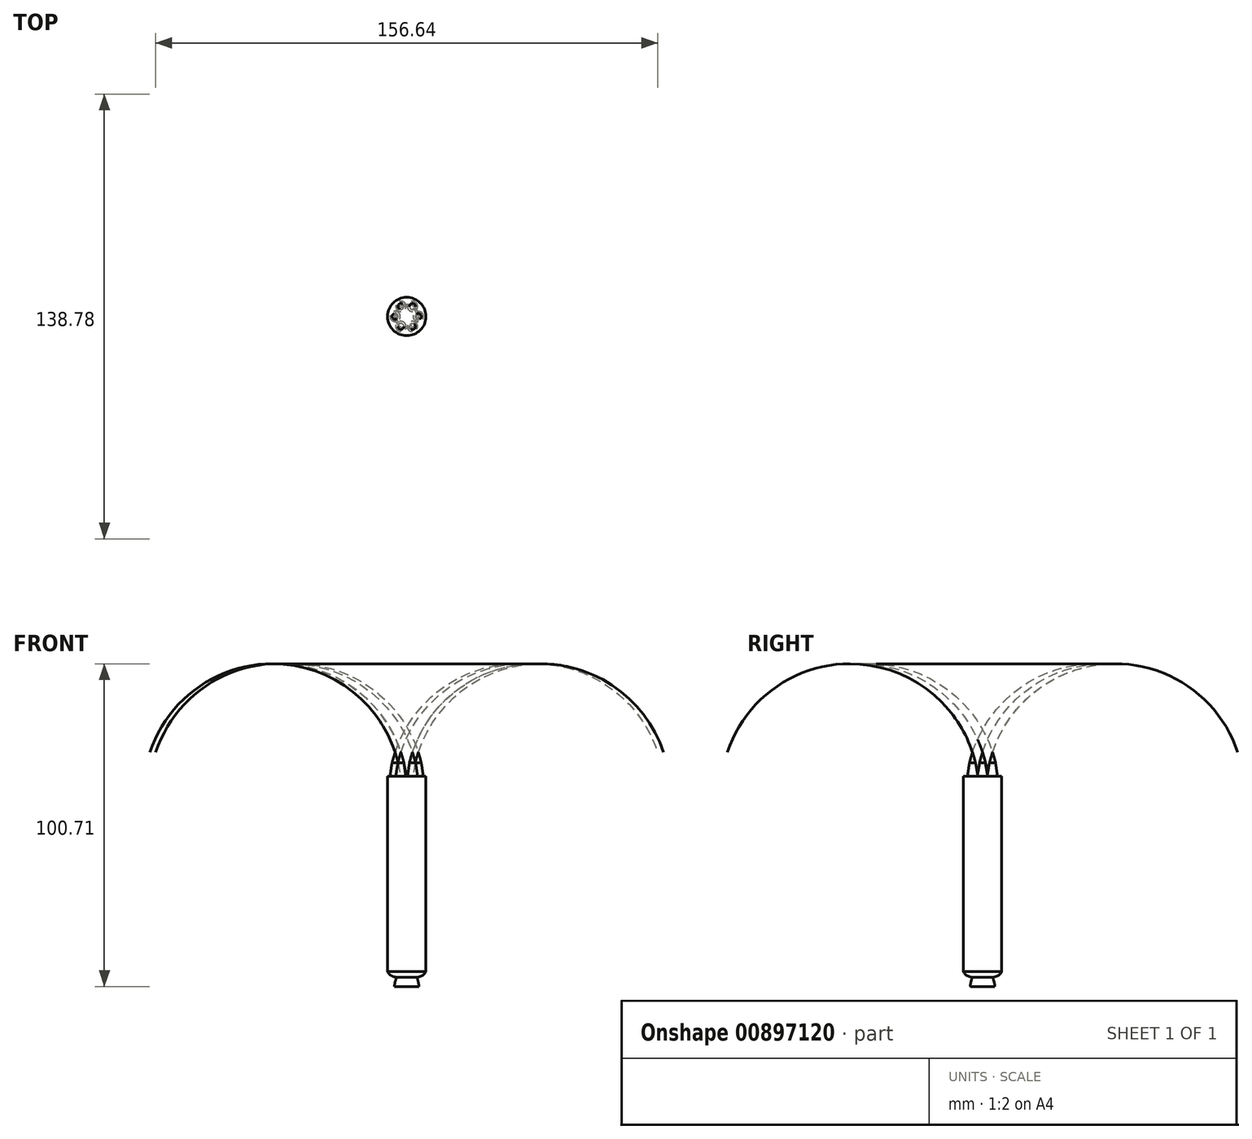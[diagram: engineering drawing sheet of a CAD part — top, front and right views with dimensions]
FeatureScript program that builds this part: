
annotation { "Feature Type Name" : "Feature", "Feature Type Description" : "" }
export const myFeature = defineFeature(function(context is Context, id is Id, definition is map)
    precondition{}
    {
        {
            var Q0;
            Q0=qCreatedBy(makeId("Front.planeOp"),FACE);
            var sketch = newSketch(context, id + "F0", { "sketchPlane" : qUnion([Q0])});
            skLineSegment(sketch, "E0", {"start": v(-6.84, -46.79) * mm, "end": v(-6.84, 46.23) * mm});
            skArc(sketch, "E1", {"start": v(-0.31, 41.1) * mm, "mid": v(-2.84, 44.6) * mm, "end": v(-6.84, 46.23) * mm});
            skFitSpline(sketch, "E2", {"points": [v(-0.84, -41.76) * mm, v(-3.65, -43.58) * mm], "startDerivative": vector(-1.75, -3.7) * mm, "endDerivative": vector(-3.13, -0.64) * mm});
            skFitSpline(sketch, "E3", {"points": [v(-3.65, -43.58) * mm, v(-3.08, -46.42) * mm], "startDerivative": vector(0.76, -2) * mm, "endDerivative": vector(-0.4, -1.8) * mm});
            skFitSpline(sketch, "E4", {"points": [v(-6.84, -46.79) * mm, v(-3.08, -46.42) * mm], "startDerivative": vector(2.11, -0.25) * mm, "endDerivative": vector(1.76, 0.6) * mm});
            skLineSegment(sketch, "E5", {"start": v(-0.81, 19.23) * mm, "end": v(-6.84, 19.23) * mm});
            skLineSegment(sketch, "E6", {"start": v(-6.84, -46.42) * mm, "end": v(-3.08, -46.42) * mm});
            skLineSegment(sketch, "E7", {"start": v(-0.84, -41.76) * mm, "end": v(-0.84, 19.23) * mm});
            skSolve(sketch);
        }
        {
            var Q0;
            Q0=makeQuery(id+"F0.imprint","IMPRINT",FACE,{"disambiguationData":[TD([[makeQuery(id+"F0.imprint","IMPRINT",EDGE,{"derivedFrom":sQuery(id+"F0.wireOp",EDGE,"3bf67111-f146-45a5-a568-fcc49153348b")}),-1.0]])]});
            var Q1;
            Q1=makeQuery(id+"F0.imprint","IMPRINT",FACE,{"disambiguationData":[TD([[makeQuery(id+"F0.imprint","IMPRINT",EDGE,{"derivedFrom":sQuery(id+"F0.wireOp",EDGE,"E2")}),-1.0]])]});
            var Q2;
            Q2=sQuery(id+"F0.wireOp",EDGE,"E0");
            revolve(context, id + "F1", {"surfaceOperationType" : NewSurfaceOperationType.NEW, "entities" : qUnion([Q0, Q1]), "axis" : qUnion([Q2]), "revolveType" : RevolveType.FULL});
        }
        {
            var Q0;
            Q0=makeQuery(id+"F1.opRevolve","SWEPT_FACE",FACE,{"disambiguationData":[OSD([sQuery(id+"F0.wireOp",EDGE,"E5")])]});
            var sketch = newSketch(context, id + "F2", { "sketchPlane" : qUnion([Q0])});
            skCircle(sketch, "E8", {"center": v(-6.84, 0.02) * mm, "radius": 6.5 * mm});
            skPoint(sketch, "E8.first.point", {"position": v(-13.33, -0.33) * mm});
            skPoint(sketch, "E8.second.point", {"position": v(-0.35, 0.35) * mm});
            skPoint(sketch, "E8.third.point", {"position": v(-0.56, -1.64) * mm});
            skCircle(sketch, "E9", {"center": v(-10.47, 0.02) * mm, "radius": 1.6 * mm});
            skCircle(sketch, "E10.1.0", {"center": v(-8.66, -3.12) * mm, "radius": 1.6 * mm});
            skCircle(sketch, "E10.2.0", {"center": v(-5.02, -3.12) * mm, "radius": 1.6 * mm});
            skCircle(sketch, "E10.3.0", {"center": v(-3.2, 0.02) * mm, "radius": 1.6 * mm});
            skCircle(sketch, "E10.4.0", {"center": v(-5.02, 3.17) * mm, "radius": 1.6 * mm});
            skCircle(sketch, "E10.5.0", {"center": v(-8.66, 3.17) * mm, "radius": 1.6 * mm});
            skPoint(sketch, "E11", {"position": v(-6.84, 0) * mm});
            skSolve(sketch);
        }
        {
            var Q0;
            Q0=sQuery(id+"F2.wireOp",EDGE,"E10.1.0");
            cPlane(context, id + "F3", {"entities" : qUnion([Q0]), "cplaneType" : CPlaneType.LINE_ANGLE, "offset" : 25 * mm, "angle" : 5 * degree, "width" : 150 * mm, "height" : 150 * mm});
        }
        {
            var Q0;
            Q0=qCreatedBy(id+"F3.planeOp",FACE);
            var sketch = newSketch(context, id + "F4", { "sketchPlane" : qUnion([Q0])});
            skLineSegment(sketch, "E12.0.0", {"start": v(-3.97, 19.23) * mm, "end": v(-0.75, 19.23) * mm});
            skLineSegment(sketch, "E13", {"start": v(-2.36, 19.23) * mm, "end": v(-2.36, 21.27) * mm});
            skLineSegment(sketch, "E14", {"start": v(-2.36, 21.27) * mm, "end": v(-2.36, 22.63) * mm});
            skLineSegment(sketch, "E15", {"start": v(-2.36, 22.63) * mm, "end": v(-2.36, 29.1) * mm});
            skLineSegment(sketch, "E16", {"start": v(-2.36, 29.1) * mm, "end": v(-3.97, 19.23) * mm});
            skArc(sketch, "E17", {"start": v(-2.36, 26.66) * mm, "mid": v(-2.86, 25.04) * mm, "end": v(-3.29, 23.4) * mm});
            skSolve(sketch);
        }
        {
            var Q0;
            {var subQ2=sQuery(id+"F4.wireOp",EDGE,"E13");Q0=makeQuery(id+"F4.imprint","IMPRINT",FACE,{"disambiguationData":[TD([[makeQuery(id+"F4.imprint","IMPRINT",EDGE,{"derivedFrom":subQ2}),1.0]])]});}
            var Q1;
            Q1=sQuery(id+"F4.wireOp",EDGE,"E13");
            revolve(context, id + "F5", {"surfaceOperationType" : NewSurfaceOperationType.NEW, "entities" : qUnion([Q0]), "axis" : qUnion([Q1]), "revolveType" : RevolveType.FULL});
        }
        {
            var Q0;
            Q0=makeQuery(id+"F5.opRevolve","SWEPT_BODY",BODY,{"disambiguationData":[OSD([sQuery(id+"F4.wireOp",EDGE,"E12.0.0"),sQuery(id+"F4.wireOp",EDGE,"E13"),sQuery(id+"F4.wireOp",EDGE,"E14"),sQuery(id+"F4.wireOp",EDGE,"E15"),sQuery(id+"F4.wireOp",EDGE,"E16")])]});
            var Q1;
            Q1=sQuery(id+"F0.wireOp",EDGE,"E0");
            circularPattern(context, id + "F6", {"entities" : qUnion([Q0]), "axis" : qUnion([Q1]), "angle" : 360 * degree, "instanceCount" : 6, "equalSpace" : true});
        }
    });
